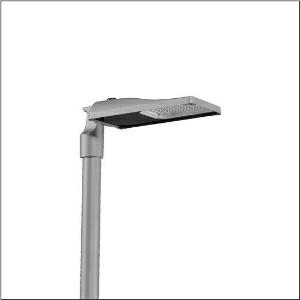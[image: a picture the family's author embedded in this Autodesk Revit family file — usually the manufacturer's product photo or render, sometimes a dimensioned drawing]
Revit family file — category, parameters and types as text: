
# Revit family: streetlight_sl_31_mini___st1_0a_5xh6d31s08ja_925e
name_source: partatom
category: Lighting Fixtures
units: mm (PartAtom-declared; Revit-internal decimal feet)

## family parameters
Cut with Voids When Loaded = No
Host = Face
Light Source = No
Part Type = Normal
Room Calculation Point = No
Round Connector Dimension = Use Diameter
Shared = No

## types (1)
- --- (1 x LED, 12270 lm, 82.5 W, 3000K)
    Apparent Load = 83 VA
    CIE Flux Codes = 40 73 97 100 100
    Color Rendering = 70
    Color Temperature = 3000K
    Default Elevation = 1800 mm
    Description = Streetlight SL 31 mini D4i, Desk-Remote mast luminaire for post-top, side-entry; light control with lens of PMMA; light distribution: ST1.0a, direct asymmetric distribution, for standard-compliant lighting for roads and squares; LED: luminous flux: 12.270lm, light colour: 730, colour temperature: 3000K; luminous efficacy: 148,7lm/W; control: pre-setting: logarithmic dimming characteristic, flexible luminous flux parameterisation, time-dependent luminous flux control, constant luminous flux control, power reduction, intelligent temperature release in ECG and LED module, overheat protection; luminaire housing, of diecast aluminium, Siteco® metallic grey (DB 702S), corrosivity category C5 high according to DIN EN ISO 12944; cover of toughened safety glass, transparent, opened without tools; mast flange of diecast aluminium, Siteco® metallic grey (DB 702S), spigot size: 76/60mm, mast flange included unmounted; with cable H07RN-F 2x 1.5mm², cable length: 10,5m, connection cable pre-assembled; mains connection: 220..240V, AC, 50/60Hz; power consumption (at start of service life): 82,5W / (at end of service life): 90,1W / (with reduced operation 50%): 36,8W; protection rating (complete): IP66; insulation class (complete): insulation class II (safety insulation); impact resistance: IK10; certification: CE, ENEC, ENEC+, VDE, UKCA, ZD4i; permissible operating ambient temperature for outdoor applications: -40..+50°C; packaging unit: 1 piece

Light Distribution: ST1.0a
    Height = 76 mm
    Lamp = 1 x LED
    Lamp Light Flux = 12270 lm
    Lamp Power = 82.5 W
    Lamp count = 1
    Length = 547 mm
    Luminous efficacy = 149 lm/W
    Manufacturer = Siteco
    ModVariant = No
    Model = 5XH6D31S08JA
    Number of Poles = 1
    OnlyDefault = Yes
    Power Factor = 1
    Product Name = Streetlight SL 31 mini | ST1.0a
    Product group = mast luminaire | pylon top
    ProductGroupID = 6100
    Protection Class = Protection class II
    Protection Degree = IP 66
    RLX_Detail_Level = 1
    RLX_Emergency_Light_Flux = 0 lm
    RLX_Emergency_Type = 0
    RLX_Emergency_Type_DB = No
    RlxData = <blob elided: 39705 chars, md5=f9c54a88>
    Socket = socket
    Standby Power = 0 W
    System Light Flux = 12270 lm
    System Power = 83 W
    Type Comments = factory setting: luminous flux: 100 % | dim-lin: 254 | 870 mA
    Type Image = l_1300330.jpg
    URL = http://relux.com
    VarID = @adj_050286
    Voltage = 0 V
    Weight = 0.00 kg
    Width = 265 mm

## geometry (parser evidence)
native form markers: Blend x4, Sweep x10
no freeform markers — native parametric forms only
